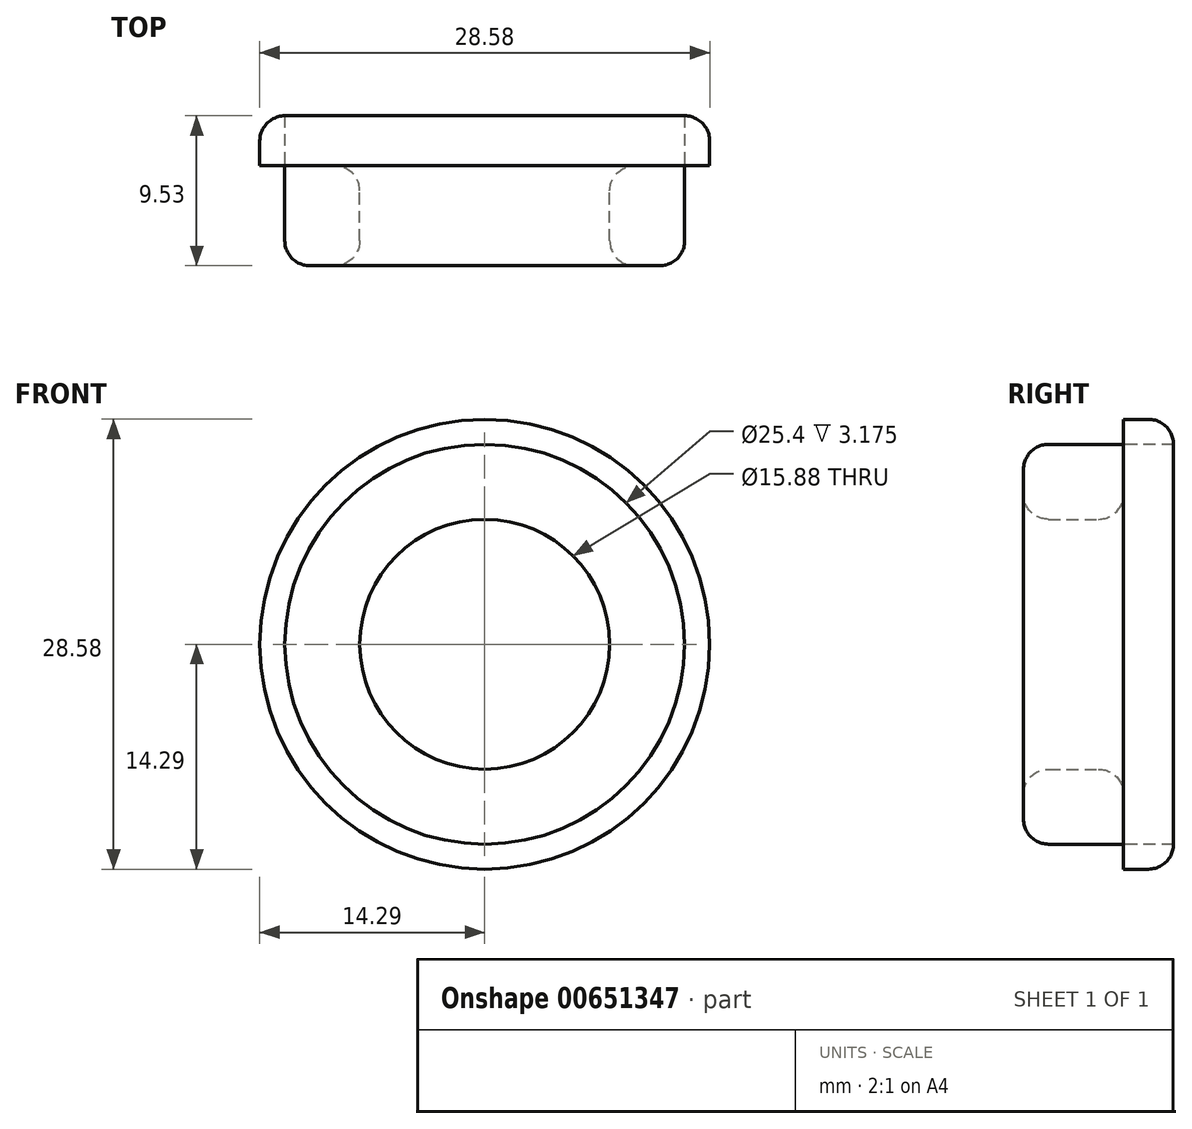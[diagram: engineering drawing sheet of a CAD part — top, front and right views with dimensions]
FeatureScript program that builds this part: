
annotation { "Feature Type Name" : "Feature", "Feature Type Description" : "" }
export const myFeature = defineFeature(function(context is Context, id is Id, definition is map)
    precondition{}
    {
        {
            var Q0;
            Q0=qCreatedBy(makeId("Front.planeOp"),FACE);
            var sketch = newSketch(context, id + "F0", { "sketchPlane" : qUnion([Q0])});
            skCircle(sketch, "E0", {"center": v(0, 0) * mm, "radius": 7.94 * mm});
            skCircle(sketch, "E1", {"center": v(0, 0) * mm, "radius": 12.7 * mm});
            skCircle(sketch, "E2", {"center": v(0, 0) * mm, "radius": 14.29 * mm});
            skSolve(sketch);
        }
        {
            var Q0;
            Q0=makeQuery(id+"F0.imprint","IMPRINT",FACE,{"disambiguationData":[TD([[makeQuery(id+"F0.imprint","IMPRINT",EDGE,{"derivedFrom":sQuery(id+"F0.wireOp",EDGE,"E0")}),-1.0]])]});
            extrude(context, id + "F1", {"entities" : qUnion([Q0]), "depth" : 6.35 * mm});
        }
        {
            var Q0;
            Q0=qSketchRegion(id+"F0",true);
            extrude(context, id + "F2", {"entities" : qUnion([Q0]), "oppositeDirection" : true, "depth" : 3.17 * mm});
        }
        {
            var Q0;
            Q0=makeQuery(id+"F1.opExtrude","CAP_EDGE",EDGE,{"disambiguationData":[OSD([sQuery(id+"F0.wireOp",EDGE,"E1")])],"isStart":false});
            var Q1;
            Q1=makeQuery(id+"F2.opExtrude","CAP_EDGE",EDGE,{"disambiguationData":[OSD([sQuery(id+"F0.wireOp",EDGE,"E2")])],"isStart":false});
            var Q2;
            Q2=makeQuery(id+"F1.opExtrude","CAP_EDGE",EDGE,{"disambiguationData":[OSD([sQuery(id+"F0.wireOp",EDGE,"E0")])],"isStart":false});
            var Q3;
            Q3=makeQuery(id+"F1.opExtrude","CAP_EDGE",EDGE,{"disambiguationData":[OSD([sQuery(id+"F0.wireOp",EDGE,"E0")])],"isStart":true});
            fillet(context, id + "F3", {"entities" : qUnion([Q0, Q1, Q2, Q3]), "radius" : 1.59 * mm, "tangentPropagation" : true, "allowEdgeOverflow" : false});
        }
    });
